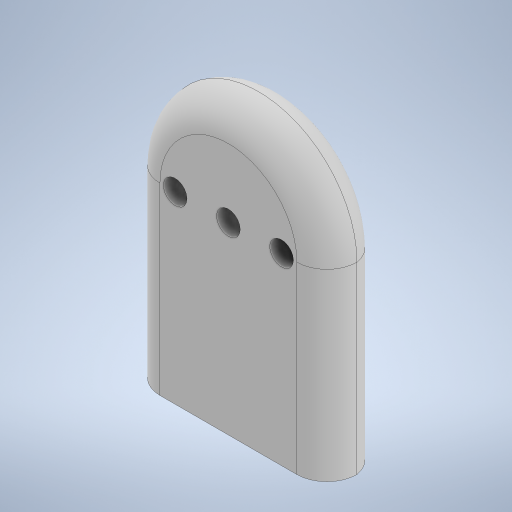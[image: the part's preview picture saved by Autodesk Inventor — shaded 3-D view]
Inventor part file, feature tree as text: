
AUTODESK INVENTOR PART (.ipt)
format: ipt  version: 2024 (Build 280153000, 153)  size: 366,080 bytes
history: native  units: in
note: dims shown in document units (in); Inventor stores cm internally (conversion verified against a paired STEP export)
features: sketch x10, extrude x9, projected_geometry x7, plane x1, fillet x1
ambient origin geometry x8: Origin, YZ Plane, XZ Plane, XY Plane, X Axis, Y Axis, Z Axis, Center Point
bodies: Solid1 (feature_tree)
feature tree (28):
  extrude  "Extrusion1"  Depth=1.25in
  extrude  "Extrusion2"  Depth=0.2756in TaperAngle=0.0deg
  extrude  "Extrusion3"  Depth=0.4921in
  plane  "Work Plane1"
  extrude  "Extrusion7"  Depth=0.1083in TaperAngle=0.0deg
  sketch  "Sketch16"  dims[d63=0.275in d64=0.275in d65=0.1181in d66=0.1181in d67=0.625in d68=0.0in d69=0.15in]
  extrude  "Extrusion11"  Depth=0.2756in TaperAngle=0.0deg
  extrude  "Extrusion12"  Depth=1.0in TaperAngle=0.0deg
  extrude  "Extrusion13"  Depth=0.0984in TaperAngle=0.0deg
  extrude  "Extrusion14"  Depth=0.1181in
  extrude  "Extrusion15"  Depth=0.275in
  fillet  "Fillet7"  Radius=0.625in
  sketch  "Sketch1"  dims[d0=0.8661in d1=1.25in]
  sketch  "Sketch3"  dims[d2=1.125in d3=0.2756in d4=0.0in]
  sketch  "Sketch4"  dims[d5=0.4921in d6=0.4921in]
  projected_geometry  "Projected Loop1"
  sketch  "Sketch7"  dims[d7=1.8898in d8=0.1083in d9=0.0in]
  projected_geometry  "Projected Loop2"
  sketch  "Sketch11"  dims[d10=0.9843in d11=0.2756in d12=0.0in]
  projected_geometry  "Projected Loop4"
  sketch  "Sketch12"  dims[d34=1.0in d35=1.0in d36=0.0in]
  projected_geometry  "Projected Loop5"
  sketch  "Sketch13"  dims[d48=0.0in d49=0.0in d50=0.0984in d51=0.0in]
  projected_geometry  "Projected Loop6"
  sketch  "Sketch14"  dims[d52=0.0in d53=0.0in d54=0.1181in d55=0.1181in d56=0.1181in]
  sketch  "Sketch15"  dims[d57=1.0in d58=0.0in d59=0.275in d60=0.275in d61=0.1181in d62=0.1181in]
  projected_geometry  "Projected Loop7"
  projected_geometry  "Projected Loop8"
